# Revit family: 306_c023674f54384127af41a8343a1dfe
name_source: partatom
category: Pipe Accessories
units: mm (PartAtom-declared; Revit-internal decimal feet)

## family parameters
Always vertical = Yes
Cut with Voids When Loaded = No
Part Type = Valve - Breaks Into
Round Connector Dimension = Use Diameter
Shared = No
Work Plane-Based = No

## types (1)
- VTA321 35-60°C 20-1,6 RP3/4
    A = 27 mm
    A__ve = -27 mm
    B = 42 mm  [stored 0.137795 ft]
    C = 52 mm  [stored 0.170604 ft]
    CAT0 = Yes
    CT2 = 16 mm
    D = 20 mm
    DT2 = 10 mm  [stored 0.0328084 ft]
    Description = Thermostatic mixing valve VTA321, PN10 internal thread
    L2D = 70 mm
    L2D_Min = 3048 mm  [stored 10 ft]
    LT2 = 35 mm  [stored 0.114829 ft]
    MC = No
    Manufacturer = ESBE
    QmdConnectorList = 301;D;302;D
    R1 = 14 mm  [stored 0.0459318 ft]
    R2 = 11 mm
    URL = http://www.esbe.eu
    W1 = 17 mm
    W2 = 16 mm
    W2D = 20 mm  [stored 0.0656168 ft]
    WT2 = 23 mm  [stored 0.0754593 ft]
    X1 = 2 mm  [stored 0.00656168 ft]
    X2 = 6 mm  [stored 0.019685 ft]
    X3 = 50 mm
    X4 = 46 mm
    Z1 = 13 mm  [stored 0.0426509 ft]
    Z1__ve = -13 mm  [stored -0.0426509 ft]
    Z2 = 3 mm  [stored 0.00984252 ft]
    magiPartTypeId = 306
    magiProductCode = VTA321 35-60°C 20-1,6 RP3/4
    magiProductFamilyId = c023674f54384127af41a8343a1dfe
    magiProductId = b7b12263d3b64bb4810d7ee8111da0

note: [stored X ft] marks values corroborated as IEEE doubles in the binary element streams (Revit-internal decimal feet)

## geometry (parser evidence)
native form markers: Sweep x2
no freeform markers — native parametric forms only
